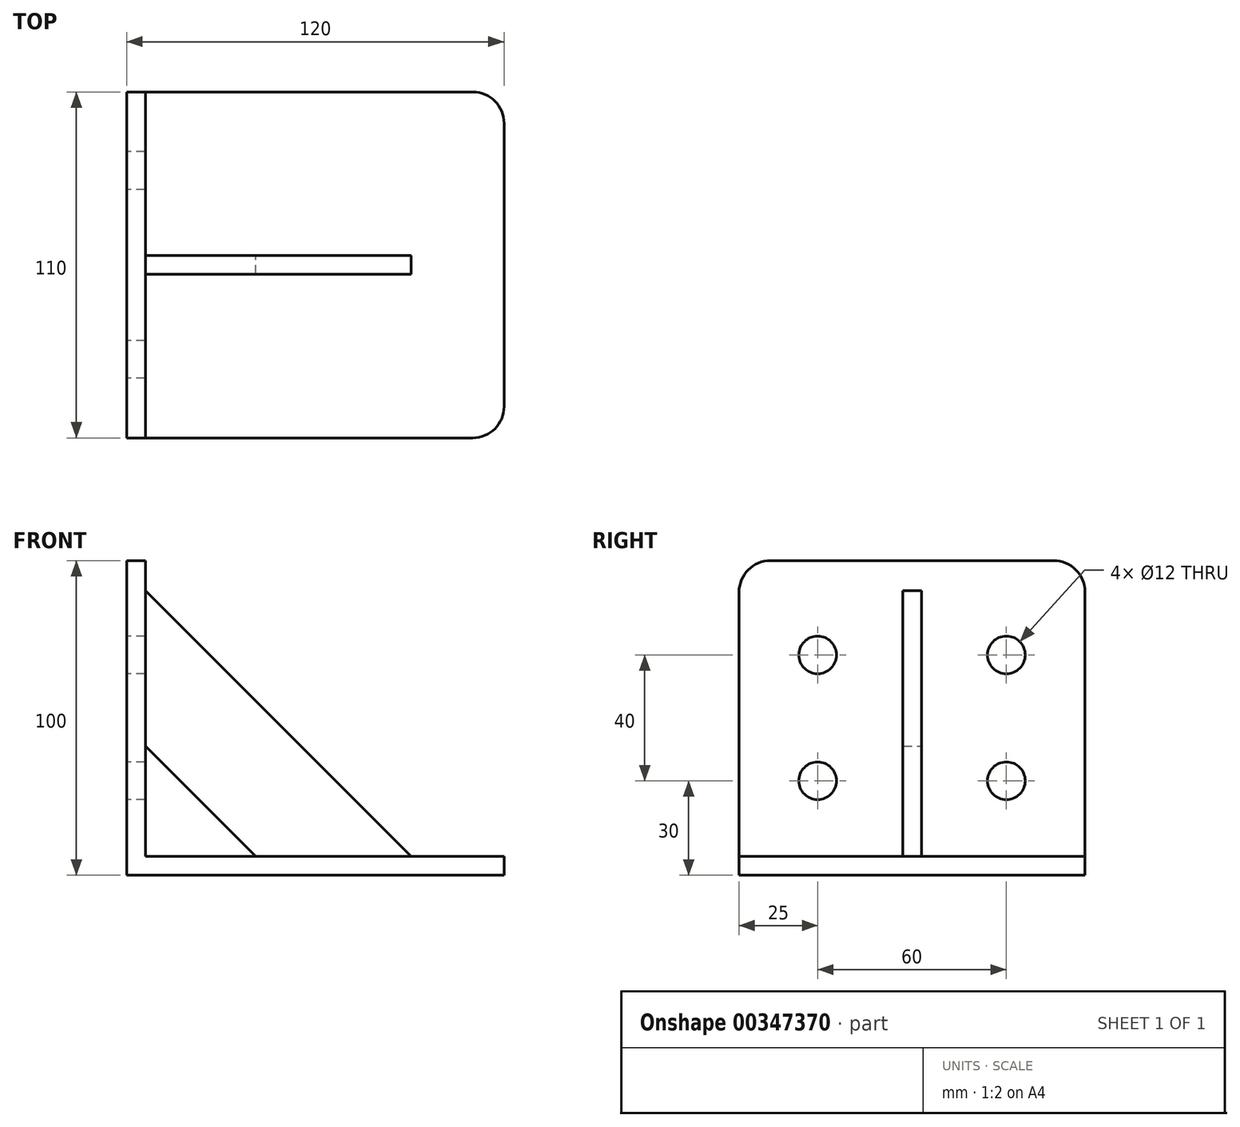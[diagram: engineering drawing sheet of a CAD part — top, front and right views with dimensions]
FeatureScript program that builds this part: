
annotation { "Feature Type Name" : "Feature", "Feature Type Description" : "" }
export const myFeature = defineFeature(function(context is Context, id is Id, definition is map)
    precondition{}
    {
        {
            var Q0;
            Q0=qCreatedBy(makeId("Front.planeOp"),FACE);
            var sketch = newSketch(context, id + "F0", { "sketchPlane" : qUnion([Q0])});
            skLineSegment(sketch, "E0", {"start": v(0, 0) * mm, "end": v(120, 0) * mm});
            skLineSegment(sketch, "E1", {"start": v(120, 6) * mm, "end": v(6, 6) * mm});
            skLineSegment(sketch, "E2", {"start": v(6, 6) * mm, "end": v(6, 100) * mm});
            skLineSegment(sketch, "E3", {"start": v(6, 100) * mm, "end": v(0, 100) * mm});
            skLineSegment(sketch, "E4", {"start": v(0, 100) * mm, "end": v(0, 0) * mm});
            skLineSegment(sketch, "E5", {"start": v(6, 41) * mm, "end": v(41, 6) * mm});
            skLineSegment(sketch, "E6.0", {"start": v(6, 90.5) * mm, "end": v(90.5, 6) * mm});
            skLineSegment(sketch, "E7", {"start": v(120, 6) * mm, "end": v(120, 0) * mm});
            skPoint(sketch, "E8.orphan", {"position": v(120, -8.43) * mm});
            skSolve(sketch);
        }
        {
            var Q0;
            Q0=makeQuery(id+"F0.imprint","IMPRINT",FACE,{"disambiguationData":[TD([[makeQuery(id+"F0.imprint","IMPRINT",EDGE,{"derivedFrom":sQuery(id+"F0.wireOp",EDGE,"E0")}),1.0]])]});
            extrude(context, id + "F1", {"entities" : qUnion([Q0]), "endBound" : BoundingType.SYMMETRIC, "depth" : 110 * mm});
        }
        {
            var Q0;
            {var subQ0=sQuery(id+"F0.wireOp",EDGE,"E5");Q0=makeQuery(id+"F0.imprint","IMPRINT",FACE,{"disambiguationData":[TD([[makeQuery(id+"F0.imprint","IMPRINT",EDGE,{"derivedFrom":subQ0}),1.0]])]});}
            extrude(context, id + "F2", {"entities" : qUnion([Q0]), "operationType" : NewBodyOperationType.ADD, "endBound" : BoundingType.SYMMETRIC, "depth" : 6 * mm});
        }
        {
            var Q0;
            Q0=makeQuery(id+"F1.opExtrude","SWEPT_FACE",FACE,{"disambiguationData":[OSD([sQuery(id+"F0.wireOp",EDGE,"E4")])]});
            var sketch = newSketch(context, id + "F3", { "sketchPlane" : qUnion([Q0])});
            skLineSegment(sketch, "E9", {"start": v(-55, 70) * mm, "end": v(55, 70) * mm, "construction": true});
            skLineSegment(sketch, "E10", {"start": v(-30, 85.76) * mm, "end": v(-30, 8.56) * mm, "construction": true});
            skLineSegment(sketch, "E11", {"start": v(30, 84.75) * mm, "end": v(30, 9.78) * mm, "construction": true});
            skCircle(sketch, "E12", {"center": v(-30, 70) * mm, "radius": 6 * mm});
            skCircle(sketch, "E13", {"center": v(30, 70) * mm, "radius": 6 * mm});
            skLineSegment(sketch, "E14", {"start": v(-49.86, 30) * mm, "end": v(48.72, 30) * mm, "construction": true});
            skCircle(sketch, "E15", {"center": v(-30, 30) * mm, "radius": 6 * mm});
            skCircle(sketch, "E16", {"center": v(30, 30) * mm, "radius": 6 * mm});
            skSolve(sketch);
        }
        {
            var Q0;
            Q0=makeQuery(id+"F3.imprint","IMPRINT",FACE,{"disambiguationData":[TD([[makeQuery(id+"F3.imprint","IMPRINT",EDGE,{"derivedFrom":sQuery(id+"F3.wireOp",EDGE,"E12")}),1.0]])]});
            var Q1;
            Q1=makeQuery(id+"F3.imprint","IMPRINT",FACE,{"disambiguationData":[TD([[makeQuery(id+"F3.imprint","IMPRINT",EDGE,{"derivedFrom":sQuery(id+"F3.wireOp",EDGE,"E13")}),1.0]])]});
            var Q2;
            Q2=makeQuery(id+"F3.imprint","IMPRINT",FACE,{"disambiguationData":[TD([[makeQuery(id+"F3.imprint","IMPRINT",EDGE,{"derivedFrom":sQuery(id+"F3.wireOp",EDGE,"E16")}),1.0]])]});
            var Q3;
            Q3=makeQuery(id+"F3.imprint","IMPRINT",FACE,{"disambiguationData":[TD([[makeQuery(id+"F3.imprint","IMPRINT",EDGE,{"derivedFrom":sQuery(id+"F3.wireOp",EDGE,"E15")}),1.0]])]});
            extrude(context, id + "F4", {"entities" : qUnion([Q0, Q1, Q2, Q3]), "operationType" : NewBodyOperationType.REMOVE, "endBound" : BoundingType.THROUGH_ALL, "oppositeDirection" : true, "depth" : 25 * mm});
        }
        {
            var Q0;
            Q0=makeQuery(id+"F1.opExtrude","CAP_EDGE",EDGE,{"disambiguationData":[OSD([sQuery(id+"F0.wireOp",EDGE,"E3")])],"isStart":false});
            var Q1;
            Q1=makeQuery(id+"F1.opExtrude","CAP_EDGE",EDGE,{"disambiguationData":[OSD([sQuery(id+"F0.wireOp",EDGE,"E7")])],"isStart":false});
            var Q2;
            Q2=makeQuery(id+"F1.opExtrude","CAP_EDGE",EDGE,{"disambiguationData":[OSD([sQuery(id+"F0.wireOp",EDGE,"E7")])],"isStart":true});
            var Q3;
            Q3=makeQuery(id+"F1.opExtrude","CAP_EDGE",EDGE,{"disambiguationData":[OSD([sQuery(id+"F0.wireOp",EDGE,"E3")])],"isStart":true});
            fillet(context, id + "F5", {"entities" : qUnion([Q0, Q1, Q2, Q3]), "radius" : 10 * mm, "tangentPropagation" : true, "allowEdgeOverflow" : false});
        }
    });
